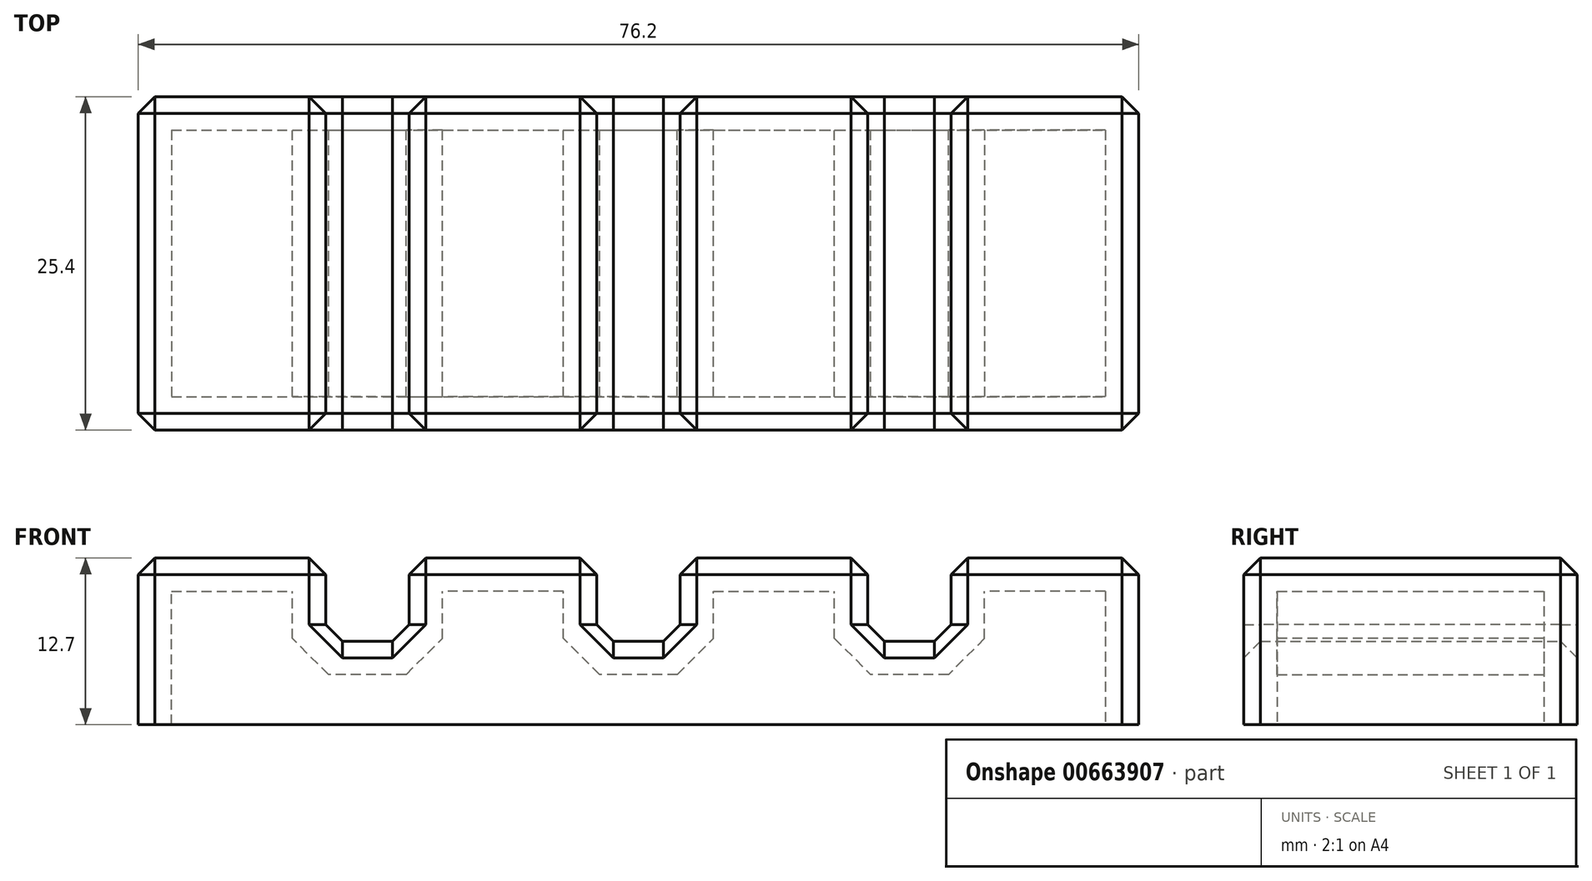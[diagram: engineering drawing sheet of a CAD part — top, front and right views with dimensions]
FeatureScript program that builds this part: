
annotation { "Feature Type Name" : "Feature", "Feature Type Description" : "" }
export const myFeature = defineFeature(function(context is Context, id is Id, definition is map)
    precondition{}
    {
        {
            var Q0;
            Q0=qCreatedBy(makeId("Top.planeOp"),FACE);
            var sketch = newSketch(context, id + "F0", { "sketchPlane" : qUnion([Q0])});
            skLineSegment(sketch, "E0.bottom", {"start": v(-38.1, 12.7) * mm, "end": v(38.1, 12.7) * mm});
            skLineSegment(sketch, "E0.top", {"start": v(-38.1, -12.7) * mm, "end": v(38.1, -12.7) * mm});
            skLineSegment(sketch, "E0.left", {"start": v(-38.1, 12.7) * mm, "end": v(-38.1, -12.7) * mm});
            skLineSegment(sketch, "E0.right", {"start": v(38.1, 12.7) * mm, "end": v(38.1, -12.7) * mm});
            skPoint(sketch, "E0.middle", {"position": v(0, 0) * mm});
            skSolve(sketch);
        }
        {
            var Q0;
            Q0 = qSketchRegion(id + "F0", true);
            extrude(context, id + "F1", {"entities" : qUnion([Q0]), "depth" : 12.7 * mm, "offsetDistance" : 25.4 * mm});
        }
        {
            var Q0;
            Q0=makeQuery(id+"F1.opExtrude","SWEPT_FACE",FACE,{"disambiguationData":[OSD([sQuery(id+"F0.wireOp",EDGE,"E0.top")])]});
            var sketch = newSketch(context, id + "F2", { "sketchPlane" : qUnion([Q0])});
            skLineSegment(sketch, "E1", {"start": v(-38.1, 6.35) * mm, "end": v(38.1, 6.35) * mm, "construction": true});
            skLineSegment(sketch, "E2.bottom", {"start": v(3.17, 6.35) * mm, "end": v(-3.18, 6.35) * mm});
            skLineSegment(sketch, "E2.top", {"start": v(3.17, 19.05) * mm, "end": v(-3.18, 19.05) * mm});
            skLineSegment(sketch, "E2.left", {"start": v(3.17, 6.35) * mm, "end": v(3.17, 19.05) * mm});
            skLineSegment(sketch, "E2.right", {"start": v(-3.18, 6.35) * mm, "end": v(-3.18, 19.05) * mm});
            skPoint(sketch, "E2.middle", {"position": v(0, 12.7) * mm});
            skLineSegment(sketch, "E3.bottom", {"start": v(23.83, 6.35) * mm, "end": v(17.48, 6.35) * mm});
            skLineSegment(sketch, "E3.top", {"start": v(23.83, 19.05) * mm, "end": v(17.48, 19.05) * mm});
            skLineSegment(sketch, "E3.left", {"start": v(23.83, 6.35) * mm, "end": v(23.83, 19.05) * mm});
            skLineSegment(sketch, "E3.right", {"start": v(17.48, 6.35) * mm, "end": v(17.48, 19.05) * mm});
            skPoint(sketch, "E3.middle", {"position": v(20.65, 12.7) * mm});
            skLineSegment(sketch, "E4.bottom", {"start": v(-17.48, 6.35) * mm, "end": v(-23.83, 6.35) * mm});
            skLineSegment(sketch, "E4.top", {"start": v(-17.48, 19.05) * mm, "end": v(-23.83, 19.05) * mm});
            skLineSegment(sketch, "E4.left", {"start": v(-17.48, 6.35) * mm, "end": v(-17.48, 19.05) * mm});
            skLineSegment(sketch, "E4.right", {"start": v(-23.83, 6.35) * mm, "end": v(-23.83, 19.05) * mm});
            skPoint(sketch, "E4.middle", {"position": v(-20.65, 12.7) * mm});
            skSolve(sketch);
        }
        {
            var Q0;
            Q0 = qSketchRegion(id + "F2", true);
            extrude(context, id + "F3", {"entities" : qUnion([Q0]), "operationType" : NewBodyOperationType.REMOVE, "endBound" : BoundingType.THROUGH_ALL, "oppositeDirection" : true, "depth" : 25.4 * mm, "offsetDistance" : 25.4 * mm});
        }
        {
            var Q0;
            {var subQ0=sQuery(id+"F0.wireOp",EDGE,"E0.bottom");var subQ1=sQuery(id+"F0.wireOp",EDGE,"E0.top");var subQ2=sQuery(id+"F0.wireOp",EDGE,"E0.left");Q0=makeQuery(id+"F3.boolean.opBoolean","SPLIT",FACE,{"disambiguationData":[TD([makeQuery(id+"F1.opExtrude","SWEPT_FACE",FACE,{"disambiguationData":[OSD([subQ2])]})])],"derivedFrom":makeQuery(id+"F1.opExtrude","CAP_FACE",FACE,{"disambiguationData":[OSD([subQ0,subQ1,subQ2,sQuery(id+"F0.wireOp",EDGE,"E0.right")])],"isStart":false})});}
            var Q1;
            {var subQ0=sQuery(id+"F0.wireOp",EDGE,"E0.bottom");var subQ1=sQuery(id+"F0.wireOp",EDGE,"E0.top");Q1=makeQuery(id+"F3.boolean.opBoolean","SPLIT",FACE,{"disambiguationData":[TD([makeQuery(id+"F3.opExtrude","SWEPT_FACE",FACE,{"disambiguationData":[OSD([sQuery(id+"F2.wireOp",EDGE,"E2.right")])]})])],"derivedFrom":makeQuery(id+"F1.opExtrude","CAP_FACE",FACE,{"disambiguationData":[OSD([subQ0,subQ1,sQuery(id+"F0.wireOp",EDGE,"E0.left"),sQuery(id+"F0.wireOp",EDGE,"E0.right")])],"isStart":false})});}
            var Q2;
            {var subQ0=sQuery(id+"F0.wireOp",EDGE,"E0.bottom");var subQ1=sQuery(id+"F0.wireOp",EDGE,"E0.top");Q2=makeQuery(id+"F3.boolean.opBoolean","SPLIT",FACE,{"disambiguationData":[TD([makeQuery(id+"F3.opExtrude","SWEPT_FACE",FACE,{"disambiguationData":[OSD([sQuery(id+"F2.wireOp",EDGE,"E2.left")])]})])],"derivedFrom":makeQuery(id+"F1.opExtrude","CAP_FACE",FACE,{"disambiguationData":[OSD([subQ0,subQ1,sQuery(id+"F0.wireOp",EDGE,"E0.left"),sQuery(id+"F0.wireOp",EDGE,"E0.right")])],"isStart":false})});}
            var Q3;
            {var subQ0=sQuery(id+"F0.wireOp",EDGE,"E0.bottom");var subQ1=sQuery(id+"F0.wireOp",EDGE,"E0.right");var subQ2=sQuery(id+"F0.wireOp",EDGE,"E0.top");Q3=makeQuery(id+"F3.boolean.opBoolean","SPLIT",FACE,{"disambiguationData":[TD([makeQuery(id+"F1.opExtrude","SWEPT_FACE",FACE,{"disambiguationData":[OSD([subQ1])]})])],"derivedFrom":makeQuery(id+"F1.opExtrude","CAP_FACE",FACE,{"disambiguationData":[OSD([subQ0,subQ2,sQuery(id+"F0.wireOp",EDGE,"E0.left"),subQ1])],"isStart":false})});}
            var Q4;
            Q4=makeQuery(id+"F3.boolean.opBoolean","COPY",FACE,{"derivedFrom":makeQuery(id+"F3.opExtrude","SWEPT_FACE",FACE,{"disambiguationData":[OSD([sQuery(id+"F2.wireOp",EDGE,"E4.bottom")])]})});
            var Q5;
            Q5=makeQuery(id+"F3.boolean.opBoolean","COPY",FACE,{"derivedFrom":makeQuery(id+"F3.opExtrude","SWEPT_FACE",FACE,{"disambiguationData":[OSD([sQuery(id+"F2.wireOp",EDGE,"E2.bottom")])]})});
            var Q6;
            Q6=makeQuery(id+"F3.boolean.opBoolean","COPY",FACE,{"derivedFrom":makeQuery(id+"F3.opExtrude","SWEPT_FACE",FACE,{"disambiguationData":[OSD([sQuery(id+"F2.wireOp",EDGE,"E3.bottom")])]})});
            var Q7;
            Q7=makeQuery(id+"F1.opExtrude","SWEPT_EDGE",EDGE,{"disambiguationData":[OSD([sQuery(id+"F0.wireOp",EDGE,"E0.top"),sQuery(id+"F0.wireOp",EDGE,"E0.left")])]});
            var Q8;
            Q8=makeQuery(id+"F1.opExtrude","SWEPT_EDGE",EDGE,{"disambiguationData":[OSD([sQuery(id+"F0.wireOp",EDGE,"E0.top"),sQuery(id+"F0.wireOp",EDGE,"E0.right")])]});
            var Q9;
            Q9=makeQuery(id+"F1.opExtrude","SWEPT_EDGE",EDGE,{"disambiguationData":[OSD([sQuery(id+"F0.wireOp",EDGE,"E0.bottom"),sQuery(id+"F0.wireOp",EDGE,"E0.right")])]});
            var Q10;
            Q10=makeQuery(id+"F1.opExtrude","SWEPT_EDGE",EDGE,{"disambiguationData":[OSD([sQuery(id+"F0.wireOp",EDGE,"E0.bottom"),sQuery(id+"F0.wireOp",EDGE,"E0.left")])]});
            chamfer(context, id + "F4", {"entities" : qUnion([Q0, Q1, Q2, Q3, Q4, Q5, Q6, Q7, Q8, Q9, Q10]), "width" : 1.27 * mm, "tangentPropagation" : true});
        }
        {
            var Q0;
            Q0=makeQuery(id+"F1.opExtrude","CAP_FACE",FACE,{"disambiguationData":[OSD([sQuery(id+"F0.wireOp",EDGE,"E0.bottom"),sQuery(id+"F0.wireOp",EDGE,"E0.top"),sQuery(id+"F0.wireOp",EDGE,"E0.left"),sQuery(id+"F0.wireOp",EDGE,"E0.right")])],"isStart":true});
            shell(context, id + "F5", {"entities" : qUnion([Q0]), "thickness" : 2.54 * mm});
        }
    });
